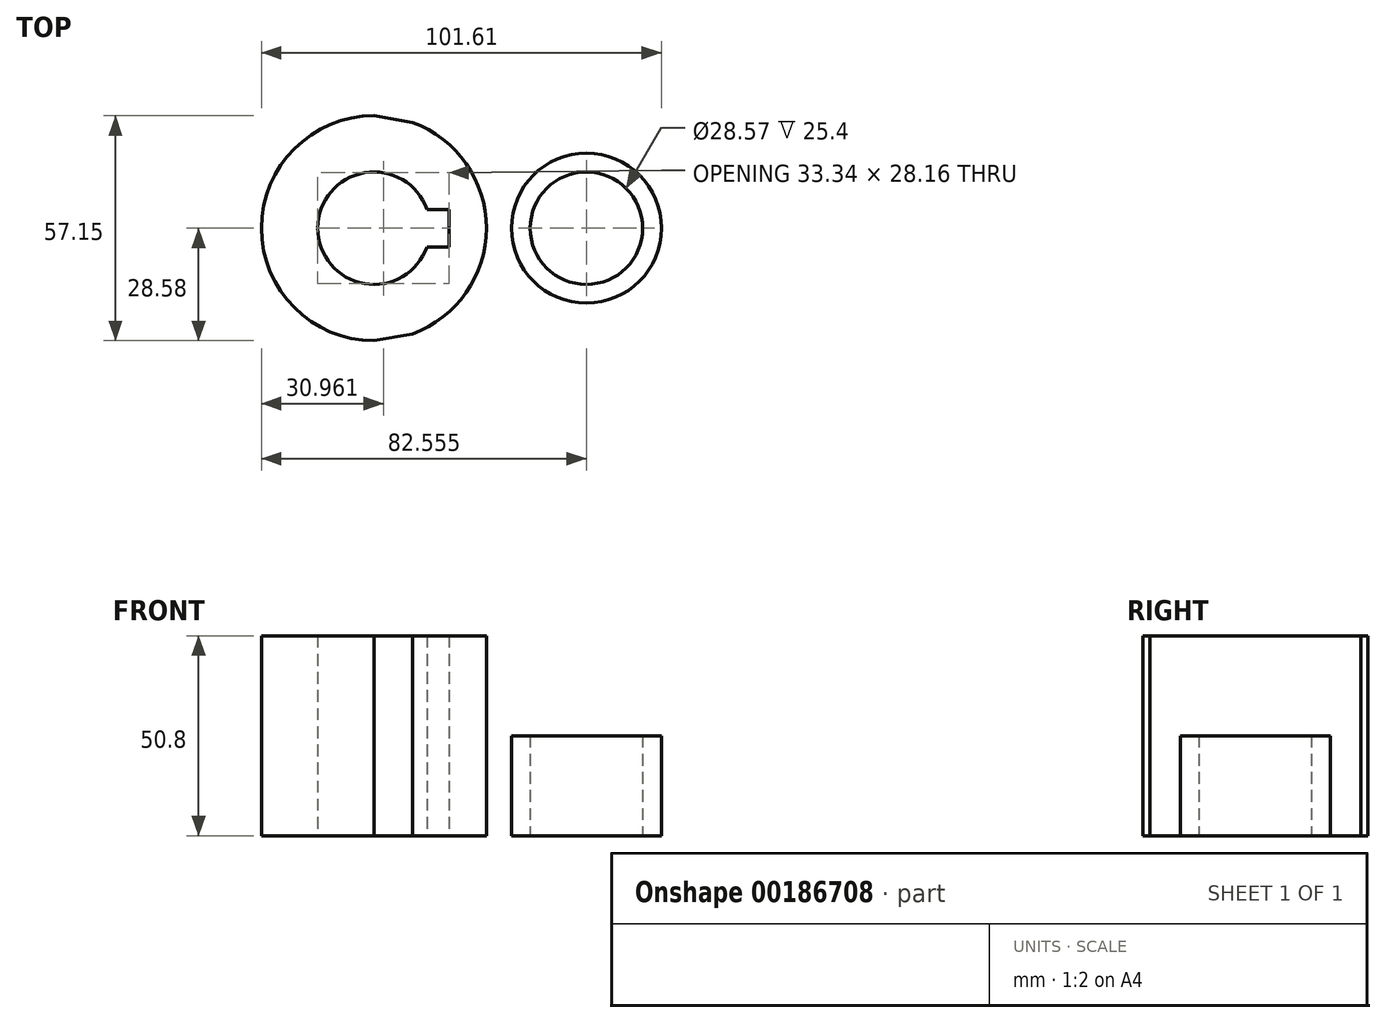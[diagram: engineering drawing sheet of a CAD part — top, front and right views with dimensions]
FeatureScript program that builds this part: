
annotation { "Feature Type Name" : "Feature", "Feature Type Description" : "" }
export const myFeature = defineFeature(function(context is Context, id is Id, definition is map)
    precondition{}
    {
        {
            var Q0;
            Q0=qCreatedBy(makeId("Top.planeOp"),FACE);
            var sketch = newSketch(context, id + "F0", { "sketchPlane" : qUnion([Q0])});
            skCircle(sketch, "E0", {"center": v(0, 0) * mm, "radius": 28.58 * mm});
            skCircle(sketch, "E1", {"center": v(53.98, 0) * mm, "radius": 19.05 * mm});
            skLineSegment(sketch, "E2", {"start": v(0, 28.57) * mm, "end": v(53.98, 19.05) * mm});
            skLineSegment(sketch, "E3", {"start": v(0, -28.57) * mm, "end": v(53.97, -19.05) * mm});
            skCircle(sketch, "E4", {"center": v(0, 0) * mm, "radius": 14.29 * mm});
            skCircle(sketch, "E5", {"center": v(53.98, 0) * mm, "radius": 14.29 * mm});
            skLineSegment(sketch, "E6.bottom", {"start": v(19.05, -4.76) * mm, "end": v(-19.05, -4.76) * mm});
            skLineSegment(sketch, "E6.top", {"start": v(19.05, 4.76) * mm, "end": v(-19.05, 4.76) * mm});
            skLineSegment(sketch, "E6.left", {"start": v(19.05, -4.76) * mm, "end": v(19.05, 4.76) * mm});
            skLineSegment(sketch, "E6.right", {"start": v(-19.05, -4.76) * mm, "end": v(-19.05, 4.76) * mm});
            skSolve(sketch);
        }
        {
            var Q0;
            {var subQ4=sQuery(id+"F0.wireOp",EDGE,"E6.left");Q0=makeQuery(id+"F0.imprint","IMPRINT",FACE,{"disambiguationData":[TD([[makeQuery(id+"F0.imprint","IMPRINT",EDGE,{"derivedFrom":subQ4}),-1.0]])]});}
            var Q1;
            {var subQ0=sQuery(id+"F0.wireOp",EDGE,"E2");var subQ1=sQuery(id+"F0.wireOp",EDGE,"E0");var subQ2=makeQuery(id+"F0.imprint","INTERSECT",VERTEX,{"disambiguationData":[OD(1.0)],"derivedFrom":[subQ1,subQ0]});Q1=makeQuery(id+"F0.imprint","IMPRINT",FACE,{"disambiguationData":[TD([[makeQuery(id+"F0.imprint","IMPRINT",EDGE,{"disambiguationData":[TD([[subQ2,1.0]])],"derivedFrom":subQ1}),-1.0]])]});}
            var Q2;
            Q2=makeQuery(id+"F0.imprint","IMPRINT",FACE,{"disambiguationData":[TD([[makeQuery(id+"F0.imprint","IMPRINT",EDGE,{"derivedFrom":sQuery(id+"F0.wireOp",EDGE,"E5")}),-1.0]])]});
            var Q3;
            {var subQ5=sQuery(id+"F0.wireOp",EDGE,"E6.right");Q3=makeQuery(id+"F0.imprint","IMPRINT",FACE,{"disambiguationData":[TD([[makeQuery(id+"F0.imprint","IMPRINT",EDGE,{"derivedFrom":subQ5}),-1.0]])]});}
            extrude(context, id + "F1", {"entities" : qUnion([Q0, Q1, Q2, Q3]), "depth" : 25.4 * mm});
        }
        {
            var Q0;
            {var subQ0=sQuery(id+"F0.wireOp",EDGE,"E2");var subQ1=sQuery(id+"F0.wireOp",EDGE,"E0");var subQ2=makeQuery(id+"F0.imprint","INTERSECT",VERTEX,{"disambiguationData":[OD(0.0)],"derivedFrom":[subQ1,subQ0]});Q0=makeQuery(id+"F0.imprint","IMPRINT",FACE,{"disambiguationData":[TD([[makeQuery(id+"F0.imprint","IMPRINT",EDGE,{"disambiguationData":[TD([[subQ2,1.0]])],"derivedFrom":subQ1}),1.0]])]});}
            var Q1;
            {var subQ0=sQuery(id+"F0.wireOp",EDGE,"E3");var subQ1=sQuery(id+"F0.wireOp",EDGE,"E0");var subQ2=makeQuery(id+"F0.imprint","INTERSECT",VERTEX,{"disambiguationData":[OD(0.0)],"derivedFrom":[subQ1,subQ0]});Q1=makeQuery(id+"F0.imprint","IMPRINT",FACE,{"disambiguationData":[TD([[makeQuery(id+"F0.imprint","IMPRINT",EDGE,{"disambiguationData":[TD([[subQ2,-1.0]])],"derivedFrom":subQ1}),1.0]])]});}
            var Q2;
            {var subQ4=sQuery(id+"F0.wireOp",EDGE,"E6.left");Q2=makeQuery(id+"F0.imprint","IMPRINT",FACE,{"disambiguationData":[TD([[makeQuery(id+"F0.imprint","IMPRINT",EDGE,{"derivedFrom":subQ4}),-1.0]])]});}
            var Q3;
            {var subQ5=sQuery(id+"F0.wireOp",EDGE,"E6.right");Q3=makeQuery(id+"F0.imprint","IMPRINT",FACE,{"disambiguationData":[TD([[makeQuery(id+"F0.imprint","IMPRINT",EDGE,{"derivedFrom":subQ5}),-1.0]])]});}
            extrude(context, id + "F2", {"entities" : qUnion([Q0, Q1, Q2, Q3]), "operationType" : NewBodyOperationType.ADD, "depth" : 50.8 * mm});
        }
    });
